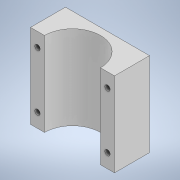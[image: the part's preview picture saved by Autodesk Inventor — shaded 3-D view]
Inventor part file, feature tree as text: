
AUTODESK INVENTOR PART (.ipt)
format: ipt  version: 2021.2 (Build 252289000, 289)  size: 479,744 bytes
history: native  units: in
note: dims shown in document units (in); Inventor stores cm internally (conversion verified against a paired STEP export)
features: sketch x4, extrude x2, hole x2
ambient origin geometry x8: Origin, YZ Plane, XZ Plane, XY Plane, X Axis, Y Axis, Z Axis, Center Point
bodies: Solid2 (feature_tree)
feature tree (8):
  extrude  "Extrusion9"  Depth=0.25in
  hole  "Hole3"  [1 undecoded]
  hole  "Hole4"  [1 undecoded]
  extrude  "Extrusion10"  Depth=0.5in
  sketch  "Sketch18"  dims[d78=2.0in d79=0.25in]
  sketch  "Sketch19"  dims[d80=0.5in d81=3.0in]
  sketch  "Sketch20"  dims[d82=0.0in d83=0.25in]
  sketch  "Sketch21"  dims[d84=0.25in d85=0.5in d86=0.5in d87=0.185in d88=0.75in d89=0.191in d90=0.219in d91=0.5635in d92=0.0625in d93=0.0in d94=0.5in d95=0.5in d96=0.5in d97=0.5in d98=0.186in d99=0.75in d100=0.204in d101=0.219in d102=0.5635in d103=0.0625in d104=0.0in d106=0.05in d107=0.0in]
note: 2 required parameter values undecoded (feature->parameter linkage not recoverable at this tier; creation-order binding heuristic only, values carry confidence <= 0.55)
